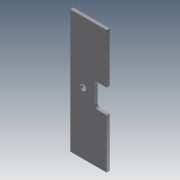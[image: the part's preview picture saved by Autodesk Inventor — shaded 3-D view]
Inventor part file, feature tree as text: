
AUTODESK INVENTOR PART (.ipt)
format: ipt  version: 2011 (Build 150239000, 239)  size: 402,432 bytes
history: native  units: in
note: dims shown in document units (in); Inventor stores cm internally (conversion verified against a paired STEP export)
features: extrude x41, sketch x41, fillet x2
ambient origin geometry x8: Origin, YZ Plane, XZ Plane, XY Plane, X Axis, Y Axis, Z Axis, Center Point
bodies: Solid1 (feature_tree)
feature tree (84):
  extrude  "Extrusion1"  Depth=4.0in
  extrude  "Extrusion2"  Depth=2.16in
  extrude  "Extrusion3"  Depth=1.7655in
  extrude  "Extrusion4"  Depth=0.029in TaperAngle=0.0deg
  extrude  "Extrusion5"  Depth=2.36in
  fillet  "Fillet1"  Radius=2.56in
  extrude  "Extrusion6"  Depth=0.125in
  extrude  "Extrusion7"  Depth=0.262in TaperAngle=0.0deg
  extrude  "Extrusion8"  Depth=0.029in TaperAngle=0.0deg
  extrude  "Extrusion9"  Depth=0.156in
  extrude  "Extrusion10"  Depth=0.5in TaperAngle=0.0deg
  extrude  "Extrusion11"  Depth=0.5in TaperAngle=0.0deg
  extrude  "Extrusion12"  Depth=1.875in TaperAngle=0.0deg
  extrude  "Extrusion13"  Depth=2.125in TaperAngle=0.0deg
  sketch  "Sketch14"  dims[d44=2.125in d45=0.0in d46=2.125in d47=0.0in]
  sketch  "Sketch15"  dims[d48=2.125in d49=0.0in d50=1.875in d51=0.0in]
  sketch  "Sketch16"  dims[d52=2.125in d53=0.0in d54=2.125in d55=0.0in]
  sketch  "Sketch17"  dims[d56=1.875in d57=0.0in d58=1.875in d59=0.0in]
  extrude  "Extrusion14"  Depth=2.125in TaperAngle=0.0deg
  extrude  "Extrusion15"  Depth=1.875in TaperAngle=0.0deg
  extrude  "Extrusion16"  Depth=2.125in TaperAngle=0.0deg
  extrude  "Extrusion17"  Depth=1.875in TaperAngle=0.0deg
  extrude  "Extrusion18"  Depth=2.125in TaperAngle=0.0deg
  extrude  "Extrusion19"  Depth=6.248in TaperAngle=0.0deg
  extrude  "Extrusion20"  Depth=1.281in
  extrude  "Extrusion21"  Depth=7.0in TaperAngle=0.0deg
  extrude  "Extrusion22"  Depth=2.0in
  extrude  "Extrusion23"  Depth=4.0in
  extrude  "Extrusion24"  Depth=2.0in
  extrude  "Extrusion25"  Depth=1.0in TaperAngle=0.0deg
  extrude  "Extrusion26"  Depth=0.25in
  extrude  "Extrusion27"  Depth=0.25in TaperAngle=0.0deg
  extrude  "Extrusion28"  Depth=0.25in TaperAngle=0.0deg
  extrude  "Extrusion29"  Depth=0.875in
  extrude  "Extrusion30"  Depth=0.5in TaperAngle=0.0deg
  extrude  "Extrusion31"  Depth=0.875in
  extrude  "Extrusion32"  Depth=0.5in TaperAngle=0.0deg
  extrude  "Extrusion33"  [1 undecoded]
  extrude  "Extrusion34"  [1 undecoded]
  fillet  "Fillet2"  [1 undecoded]
  extrude  "Extrusion35"  [1 undecoded]
  extrude  "Extrusion36"  [1 undecoded]
  extrude  "Extrusion37"  [1 undecoded]
  extrude  "Extrusion38"  [1 undecoded]
  extrude  "Extrusion39"  [1 undecoded]
  extrude  "Extrusion40"  [1 undecoded]
  extrude  "Extrusion41"  [1 undecoded]
  sketch  "Sketch1"  dims[d0=4.0in d1=4.0in]
  sketch  "Sketch2"  dims[d2=0.029in d3=0.0in d4=2.16in]
  sketch  "Sketch3"  dims[d5=0.029in d6=0.0in d7=1.7655in]
  sketch  "Sketch4"  dims[d8=0.156in d9=0.029in d10=0.0in]
  sketch  "Sketch5"  dims[d11=0.029in d12=0.0in d13=2.36in d14=2.56in]
  sketch  "Sketch6"  dims[d15=0.262in d16=0.0in d17=0.125in]
  sketch  "Sketch7"  dims[d18=0.362in d19=0.0in d20=0.262in d21=0.0in]
  sketch  "Sketch8"  dims[d22=0.1in d23=0.0in d24=0.029in d25=0.0in]
  sketch  "Sketch9"  dims[d26=1.594in d27=0.156in]
  sketch  "Sketch10"  dims[d28=0.029in d29=0.0in d30=0.5in d31=0.0in]
  sketch  "Sketch11"  dims[d32=0.75in d33=0.0in d34=0.5in d35=0.0in]
  sketch  "Sketch12"  dims[d36=2.125in d37=0.0in d38=1.875in d39=0.0in]
  sketch  "Sketch13"  dims[d40=1.875in d41=0.0in d42=2.125in d43=0.0in]
  sketch  "Sketch18"  dims[d60=2.125in d61=0.0in d62=2.125in d63=0.0in]
  sketch  "Sketch19"  dims[d64=0.875in d65=0.0in d66=6.248in d67=0.0in]
  sketch  "Sketch20"  dims[d68=7.0in d69=0.0in d70=1.281in]
  sketch  "Sketch21"  dims[d71=3.188in d72=7.0in d73=0.0in]
  sketch  "Sketch22"  dims[d74=0.25in d75=0.0in d76=2.0in]
  sketch  "Sketch23"  dims[d77=2.0in d78=4.0in]
  sketch  "Sketch24"  dims[d79=1.0in d80=0.0in d81=2.0in]
  sketch  "Sketch25"  dims[d82=1.0in d83=1.0in d84=0.0in]
  sketch  "Sketch26"  dims[d85=0.5in d86=0.25in]
  sketch  "Sketch27"  dims[d87=0.25in d88=0.25in d89=0.0in]
  sketch  "Sketch28"  dims[d90=0.25in d91=0.0in d92=0.25in d93=0.0in]
  sketch  "Sketch29"  dims[d94=0.656in d95=0.875in]
  sketch  "Sketch30"  dims[d96=0.5in d97=0.0in d98=0.5in d99=0.0in]
  sketch  "Sketch31"  dims[d100=0.875in d101=0.875in]
  sketch  "Sketch32"  dims[d102=0.5in d103=0.0in d104=0.5in d105=0.0in]
  sketch  "Sketch33"
  sketch  "Sketch34"
  sketch  "Sketch35"
  sketch  "Sketch36"
  sketch  "Sketch37"
  sketch  "Sketch38"
  sketch  "Sketch39"
  sketch  "Sketch40"
  sketch  "Sketch41"
note: 10 required parameter values undecoded (feature->parameter linkage not recoverable at this tier; creation-order binding heuristic only, values carry confidence <= 0.55)
